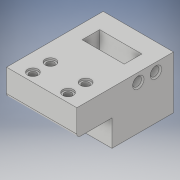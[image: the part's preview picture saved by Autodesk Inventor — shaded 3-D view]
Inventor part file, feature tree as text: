
AUTODESK INVENTOR PART (.ipt)
format: ipt  version: 2019 (Build 230136000, 136)  size: 211,968 bytes
history: native  units: mm
features: sketch x10, extrude x5, hole x5, fillet x1, mirror x1
ambient origin geometry x8: Origin, YZ Plane, XZ Plane, XY Plane, X Axis, Y Axis, Z Axis, Center Point
bodies: Solid1 (feature_tree)
feature tree (22):
  extrude  "Extrusion1"  Depth=20.0mm
  hole  "Hole1"  [1 undecoded]
  fillet  "Fillet1"  Radius=2.0mm
  extrude  "Extrusion2"  Depth=30.0mm
  extrude  "Extrusion3"  Depth=10.0mm TaperAngle=0.0deg
  hole  "Hole2"  [1 undecoded]
  hole  "Hole3"  [1 undecoded]
  extrude  "Extrusion4"  Depth=10.0mm
  extrude  "Extrusion5"  Depth=20.0mm
  hole  "Hole4"  [1 undecoded]
  hole  "Hole5"  [1 undecoded]
  mirror  "Mirror1"
  sketch  "Sketch1"  dims[d0=40.0mm d1=20.0mm]
  sketch  "Sketch2"  dims[d2=15.0mm d3=0.0mm d4=20.0mm]
  sketch  "Sketch3"  dims[d5=4.0mm d6=6.0mm d7=6.0mm d8=1.0mm d9=90.0deg d10=8.0mm d11=20.594885mm d12=2.0mm]
  sketch  "Sketch4"  dims[d13=5.0mm d14=30.0mm]
  sketch  "Sketch5"  dims[d15=15.0mm d16=0.0mm d17=10.0mm d18=0.0mm]
  sketch  "Sketch6"  dims[d19=7.5mm d20=6.0mm d21=8.4mm d22=2.3mm d23=90.0deg d24=10.0mm d25=0.0mm]
  sketch  "Sketch7"  dims[d26=19.2mm d27=6.0mm d28=8.4mm d29=2.3mm d30=90.0deg d31=6.5mm d32=0.0mm d33=8.0mm]
  sketch  "Sketch8"  dims[d34=10.0mm d35=0.0mm d36=10.0mm d37=0.0mm]
  sketch  "Sketch9"  dims[d38=7.5mm d39=6.0mm d40=19.2mm d41=6.0mm d42=90.0deg d43=6.5mm d44=0.0mm d45=10.0mm]
  sketch  "Sketch10"  dims[d46=5.0mm d47=20.0mm d48=5.0mm d49=6.0mm d50=6.5mm d51=6.0mm d52=90.0deg d53=6.0mm d54=20.594885mm d55=1.0mm d56=1.0mm d57=6.0mm d58=6.5mm d59=5.0mm d60=5.0mm d61=14.3117mm d62=0.75mm d63=20.594885mm d64=0.0625mm d65=0.75mm d66=0.375mm]
note: 5 required parameter values undecoded (feature->parameter linkage not recoverable at this tier; creation-order binding heuristic only, values carry confidence <= 0.55)
